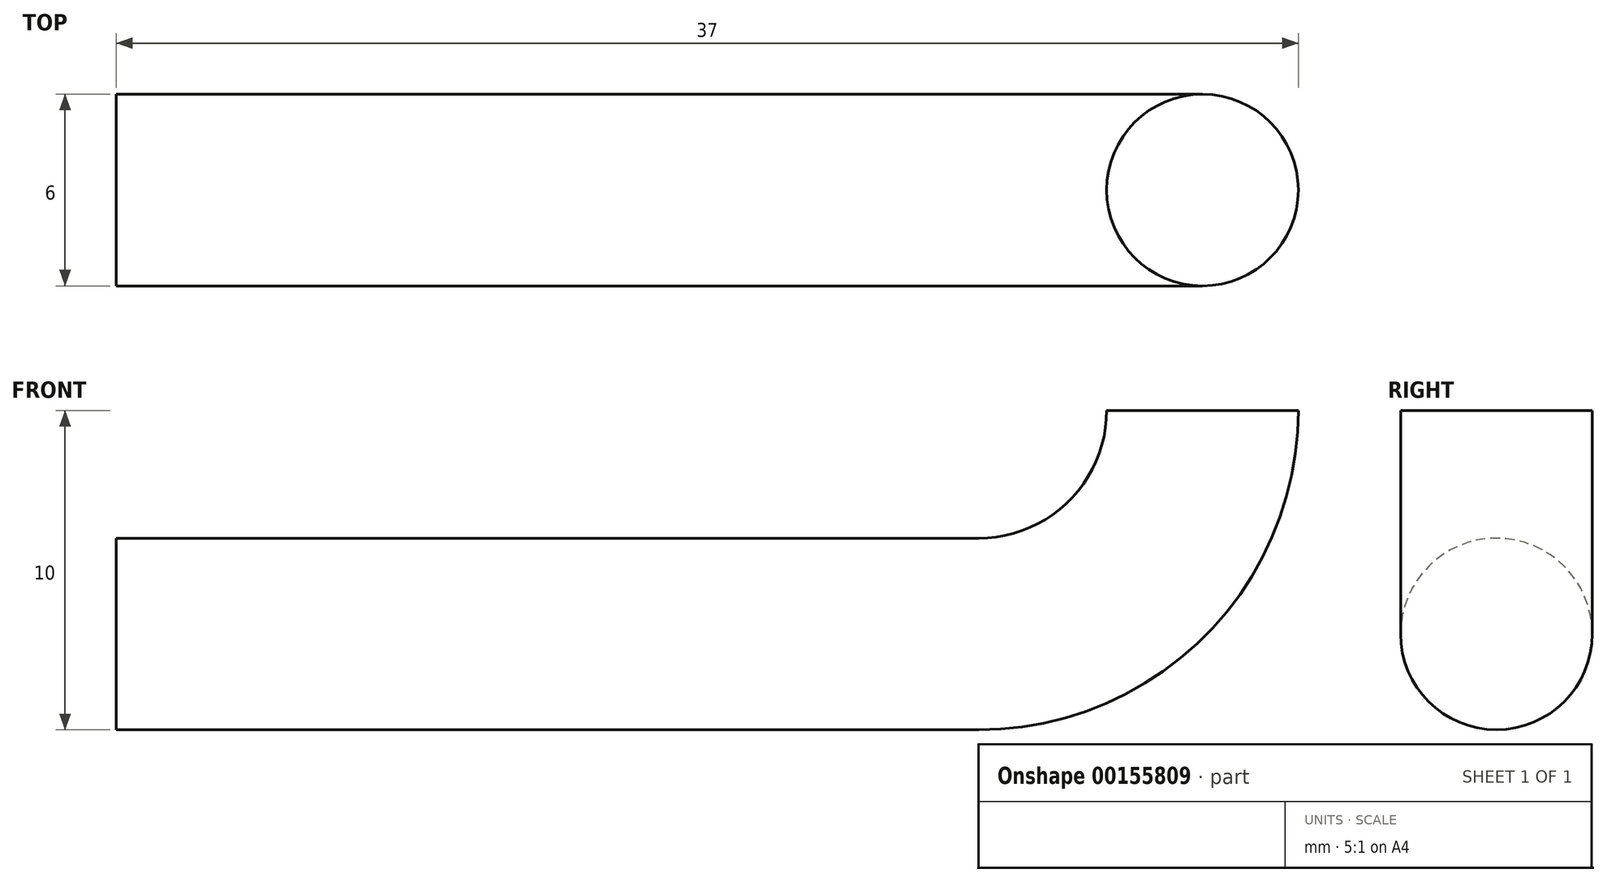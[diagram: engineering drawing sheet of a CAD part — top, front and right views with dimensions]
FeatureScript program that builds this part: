
annotation { "Feature Type Name" : "Feature", "Feature Type Description" : "" }
export const myFeature = defineFeature(function(context is Context, id is Id, definition is map)
    precondition{}
    {
        {
            var Q0;
            Q0=qCreatedBy(makeId("Front.planeOp"),FACE);
            var sketch = newSketch(context, id + "F0", { "sketchPlane" : qUnion([Q0])});
            skLineSegment(sketch, "E0", {"start": v(0, 0) * mm, "end": v(27, 0) * mm});
            skArc(sketch, "E1", {"start": v(27, 0) * mm, "mid": v(31.95, 2.05) * mm, "end": v(34, 7) * mm});
            skSolve(sketch);
        }
        {
            var Q0;
            Q0=qCreatedBy(makeId("Right.planeOp"),FACE);
            var sketch = newSketch(context, id + "F1", { "sketchPlane" : qUnion([Q0])});
            skCircle(sketch, "E2", {"center": v(0, 0) * mm, "radius": 3 * mm});
            skSolve(sketch);
        }
        {
            var Q0;
            Q0=makeQuery(id+"F1.imprint","IMPRINT",FACE,{"disambiguationData":[TD([[makeQuery(id+"F1.imprint","IMPRINT",EDGE,{"derivedFrom":sQuery(id+"F1.wireOp",EDGE,"E2")}),1.0]])]});
            var Q1;
            Q1=sQuery(id+"F0.wireOp",EDGE,"ev8xvnma-Kx5n-LJW8-0ofH-jus9e5lSajr3");
            var Q2;
            Q2=sQuery(id+"F0.wireOp",EDGE,"E0");
            var Q3;
            Q3=sQuery(id+"F0.wireOp",EDGE,"E1");
            var Q4;
            Q4=sQuery(id+"F0.wireOp",EDGE,"Uknd1tQH-TghJ-cEOa-DVhq-kFCsb7NGiCwg");
            var Q5;
            Q5=sQuery(id+"F0.wireOp",EDGE,"2TiX2ViZ-t8sK-9hUQ-MlfC-gPFm1rc3iv9g");
            sweep(context, id + "F2", {"profiles" : qUnion([Q0]), "path" : qUnion([Q1, Q2, Q3, Q4, Q5])});
        }
    });
